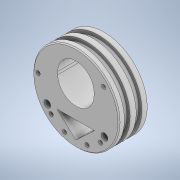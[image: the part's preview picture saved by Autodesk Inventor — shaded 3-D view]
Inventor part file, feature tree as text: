
AUTODESK INVENTOR PART (.ipt)
format: ipt  version: 2020 (Build 240168000, 168)  size: 353,280 bytes
history: native  units: in
note: dims shown in document units (in); Inventor stores cm internally (conversion verified against a paired STEP export)
features: sketch x13, extrude x12, projected_geometry x4, plane x3, fillet x1, chamfer x1
ambient origin geometry x8: Origin, YZ Plane, XZ Plane, XY Plane, X Axis, Y Axis, Z Axis, Center Point
bodies: Solid1 (feature_tree)
feature tree (34):
  extrude  "Extrusion1"  Depth=1.1in TaperAngle=0.0deg
  plane  "Work Plane1"
  extrude  "Extrusion2"  Depth=0.11in
  plane  "Work Plane2"
  extrude  "Extrusion3"  [1 undecoded]
  extrude  "Extrusion4"  Depth=0.195in TaperAngle=0.0deg
  extrude  "Extrusion5"  Depth=0.235in
  extrude  "Extrusion6"  Depth=0.14in
  fillet  "Fillet1"  Radius=0.14in
  chamfer  "Chamfer1"  [1 undecoded]
  extrude  "Extrusion9"  Depth=0.5in
  extrude  "Extrusion10"  TaperAngle=0.0deg  [1 undecoded]
  extrude  "Extrusion11"  Depth=0.5in
  plane  "Work Plane4"
  extrude  "Extrusion12"  Depth=0.5in TaperAngle=45.0deg
  extrude  "Extrusion13"  Depth=0.5in
  sketch  "Sketch15"  dims[d25=0.5in d26=0.65in]
  extrude  "Extrusion14"  Depth=0.5in
  sketch  "Sketch1"  dims[d0=2.972in d1=1.1in d2=0.0in]
  sketch  "Sketch2"  dims[d3=-0.25in d4=0.11in]
  sketch  "Sketch3"  dims[d5=0.195in d6=0.0in d7=-0.25in]
  sketch  "Sketch4"  dims[d8=0.11in d9=0.195in d10=0.0in]
  sketch  "Sketch5"  dims[d11=1.55in d12=0.235in]
  sketch  "Sketch6"  dims[d13=0.0in d14=0.0in d16=0.14in d17=0.14in]
  projected_geometry  "Projected Loop1"
  sketch  "Sketch9"  dims[d18=0.14in]
  sketch  "Sketch11"  dims[d19=0.82in]
  projected_geometry  "Projected Loop4"
  sketch  "Sketch12"  dims[d20=0.955in]
  projected_geometry  "Projected Loop5"
  sketch  "Sketch13"  dims[d21=0.9in]
  projected_geometry  "Projected Loop6"
  sketch  "Sketch14"  dims[d22=0.85in d23=0.0in d24=0.0in]
  sketch  "Sketch16"  dims[d27=0.65in d28=0.0in d29=0.0in d33=0.125in d34=0.1in d35=0.125in d36=45.0deg d45=0.14in d46=0.14in d47=0.778in d48=1.175in d49=0.225in d50=0.14in d51=1.345in d52=0.0in d53=0.0in d54=0.065in d55=0.0in d56=0.065in d57=0.0in d60=0.75in d61=0.25in d62=1.0in d63=0.0in d64=0.14in d65=0.1in d66=1.3in d67=0.233in d68=0.233in d69=0.0in d70=0.0in d71=1.25in d73=0.425in d75=0.625in d76=0.1in d77=0.0in d78=0.0in d30=0.5in d31=0.0344in]
note: 3 required parameter values undecoded (feature->parameter linkage not recoverable at this tier; creation-order binding heuristic only, values carry confidence <= 0.55)
